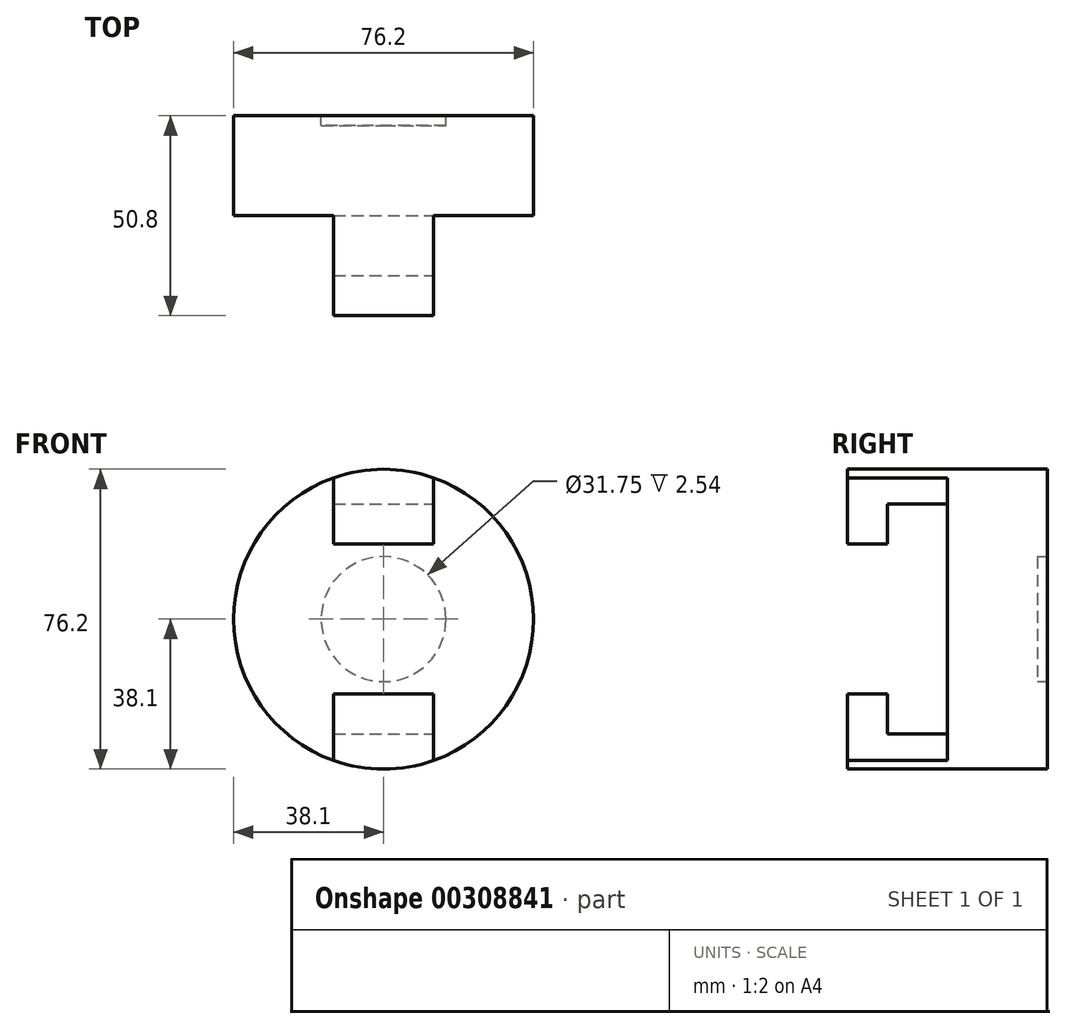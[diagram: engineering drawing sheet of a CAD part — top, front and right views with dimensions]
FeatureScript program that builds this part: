
annotation { "Feature Type Name" : "Feature", "Feature Type Description" : "" }
export const myFeature = defineFeature(function(context is Context, id is Id, definition is map)
    precondition{}
    {
        {
            var Q0;
            Q0=qCreatedBy(makeId("Front.planeOp"),FACE);
            var sketch = newSketch(context, id + "F0", { "sketchPlane" : qUnion([Q0])});
            skCircle(sketch, "E0", {"center": v(0, 0) * mm, "radius": 38.1 * mm});
            skSolve(sketch);
        }
        {
            var Q0;
            Q0=makeQuery(id+"F0.imprint","IMPRINT",FACE,{"disambiguationData":[TD([[makeQuery(id+"F0.imprint","IMPRINT",EDGE,{"derivedFrom":sQuery(id+"F0.wireOp",EDGE,"E0")}),1.0]])]});
            extrude(context, id + "F1", {"entities" : qUnion([Q0]), "depth" : 25.4 * mm});
        }
        {
            var Q0;
            Q0=makeQuery(id+"F1.opExtrude","CAP_FACE",FACE,{"disambiguationData":[OSD([sQuery(id+"F0.wireOp",EDGE,"E0")])],"isStart":false});
            var sketch = newSketch(context, id + "F2", { "sketchPlane" : qUnion([Q0])});
            skLineSegment(sketch, "E1", {"start": v(0, 38.1) * mm, "end": v(0, 19.05) * mm});
            skLineSegment(sketch, "E2", {"start": v(0, -38.1) * mm, "end": v(0, -19.05) * mm});
            skLineSegment(sketch, "E3", {"start": v(0, -19.05) * mm, "end": v(-12.7, -19.05) * mm});
            skLineSegment(sketch, "E4", {"start": v(-12.7, -19.05) * mm, "end": v(12.7, -19.05) * mm});
            skLineSegment(sketch, "E5", {"start": v(-12.7, -19.05) * mm, "end": v(-12.7, -35.92) * mm});
            skLineSegment(sketch, "E6", {"start": v(12.7, -19.05) * mm, "end": v(12.7, -35.92) * mm});
            skLineSegment(sketch, "E7", {"start": v(-12.7, 19.05) * mm, "end": v(12.7, 19.05) * mm});
            skLineSegment(sketch, "E8", {"start": v(-12.7, 19.05) * mm, "end": v(-12.7, 35.92) * mm});
            skLineSegment(sketch, "E9", {"start": v(12.7, 19.05) * mm, "end": v(12.7, 35.92) * mm});
            skSolve(sketch);
        }
        {
            var Q0;
            {var subQ0=sQuery(id+"F2.wireOp",EDGE,"E1");Q0=makeQuery(id+"F2.imprint","IMPRINT",FACE,{"disambiguationData":[TD([[makeQuery(id+"F2.imprint","IMPRINT",EDGE,{"derivedFrom":subQ0}),-1.0]])]});}
            var Q1;
            {var subQ0=sQuery(id+"F2.wireOp",EDGE,"E1");Q1=makeQuery(id+"F2.imprint","IMPRINT",FACE,{"disambiguationData":[TD([[makeQuery(id+"F2.imprint","IMPRINT",EDGE,{"derivedFrom":subQ0}),1.0]])]});}
            var Q2;
            {var subQ0=sQuery(id+"F2.wireOp",EDGE,"E2");Q2=makeQuery(id+"F2.imprint","IMPRINT",FACE,{"disambiguationData":[TD([[makeQuery(id+"F2.imprint","IMPRINT",EDGE,{"derivedFrom":subQ0}),1.0]])]});}
            var Q3;
            {var subQ0=sQuery(id+"F2.wireOp",EDGE,"E2");Q3=makeQuery(id+"F2.imprint","IMPRINT",FACE,{"disambiguationData":[TD([[makeQuery(id+"F2.imprint","IMPRINT",EDGE,{"derivedFrom":subQ0}),-1.0]])]});}
            extrude(context, id + "F3", {"entities" : qUnion([Q0, Q1, Q2, Q3]), "operationType" : NewBodyOperationType.ADD, "depth" : 25.4 * mm});
        }
        {
            var Q0;
            Q0=makeQuery(id+"F3.opExtrude","SWEPT_FACE",FACE,{"disambiguationData":[OSD([sQuery(id+"F2.wireOp",EDGE,"E9")])]});
            var sketch = newSketch(context, id + "F4", { "sketchPlane" : qUnion([Q0])});
            skLineSegment(sketch, "E10.bottom", {"start": v(-25.4, 19.05) * mm, "end": v(-40.64, 19.05) * mm});
            skLineSegment(sketch, "E10.top", {"start": v(-25.4, 29.21) * mm, "end": v(-40.64, 29.21) * mm});
            skLineSegment(sketch, "E10.left", {"start": v(-25.4, 19.05) * mm, "end": v(-25.4, 29.21) * mm});
            skLineSegment(sketch, "E10.right", {"start": v(-40.64, 19.05) * mm, "end": v(-40.64, 29.21) * mm});
            skSolve(sketch);
        }
        {
            var Q0;
            Q0=makeQuery(id+"F4.imprint","IMPRINT",FACE,{"disambiguationData":[TD([[makeQuery(id+"F4.imprint","IMPRINT",EDGE,{"derivedFrom":sQuery(id+"F4.wireOp",EDGE,"E10.bottom")}),1.0]])]});
            extrude(context, id + "F5", {"entities" : qUnion([Q0]), "operationType" : NewBodyOperationType.REMOVE, "oppositeDirection" : true, "depth" : 25.4 * mm});
        }
        {
            var Q0;
            Q0=makeQuery(id+"F3.opExtrude","SWEPT_FACE",FACE,{"disambiguationData":[OSD([sQuery(id+"F2.wireOp",EDGE,"E6")])]});
            var sketch = newSketch(context, id + "F6", { "sketchPlane" : qUnion([Q0])});
            skLineSegment(sketch, "E11.bottom", {"start": v(-25.4, -19.05) * mm, "end": v(-40.64, -19.05) * mm});
            skLineSegment(sketch, "E11.top", {"start": v(-25.4, -29.21) * mm, "end": v(-40.64, -29.21) * mm});
            skLineSegment(sketch, "E11.left", {"start": v(-25.4, -19.05) * mm, "end": v(-25.4, -29.21) * mm});
            skLineSegment(sketch, "E11.right", {"start": v(-40.64, -19.05) * mm, "end": v(-40.64, -29.21) * mm});
            skSolve(sketch);
        }
        {
            var Q0;
            Q0=makeQuery(id+"F6.imprint","IMPRINT",FACE,{"disambiguationData":[TD([[makeQuery(id+"F6.imprint","IMPRINT",EDGE,{"derivedFrom":sQuery(id+"F6.wireOp",EDGE,"E11.bottom")}),-1.0]])]});
            extrude(context, id + "F7", {"entities" : qUnion([Q0]), "operationType" : NewBodyOperationType.REMOVE, "oppositeDirection" : true, "depth" : 25.4 * mm});
        }
        {
            var Q0;
            Q0=makeQuery(id+"F1.opExtrude","CAP_FACE",FACE,{"disambiguationData":[OSD([sQuery(id+"F0.wireOp",EDGE,"E0")])],"isStart":true});
            var sketch = newSketch(context, id + "F8", { "sketchPlane" : qUnion([Q0])});
            skCircle(sketch, "E12", {"center": v(0, 0) * mm, "radius": 15.88 * mm});
            skSolve(sketch);
        }
        {
            var Q0;
            Q0=makeQuery(id+"F8.imprint","IMPRINT",FACE,{"disambiguationData":[TD([[makeQuery(id+"F8.imprint","IMPRINT",EDGE,{"derivedFrom":sQuery(id+"F8.wireOp",EDGE,"E12")}),1.0]])]});
            extrude(context, id + "F9", {"entities" : qUnion([Q0]), "operationType" : NewBodyOperationType.REMOVE, "oppositeDirection" : true, "depth" : 2.54 * mm});
        }
    });
